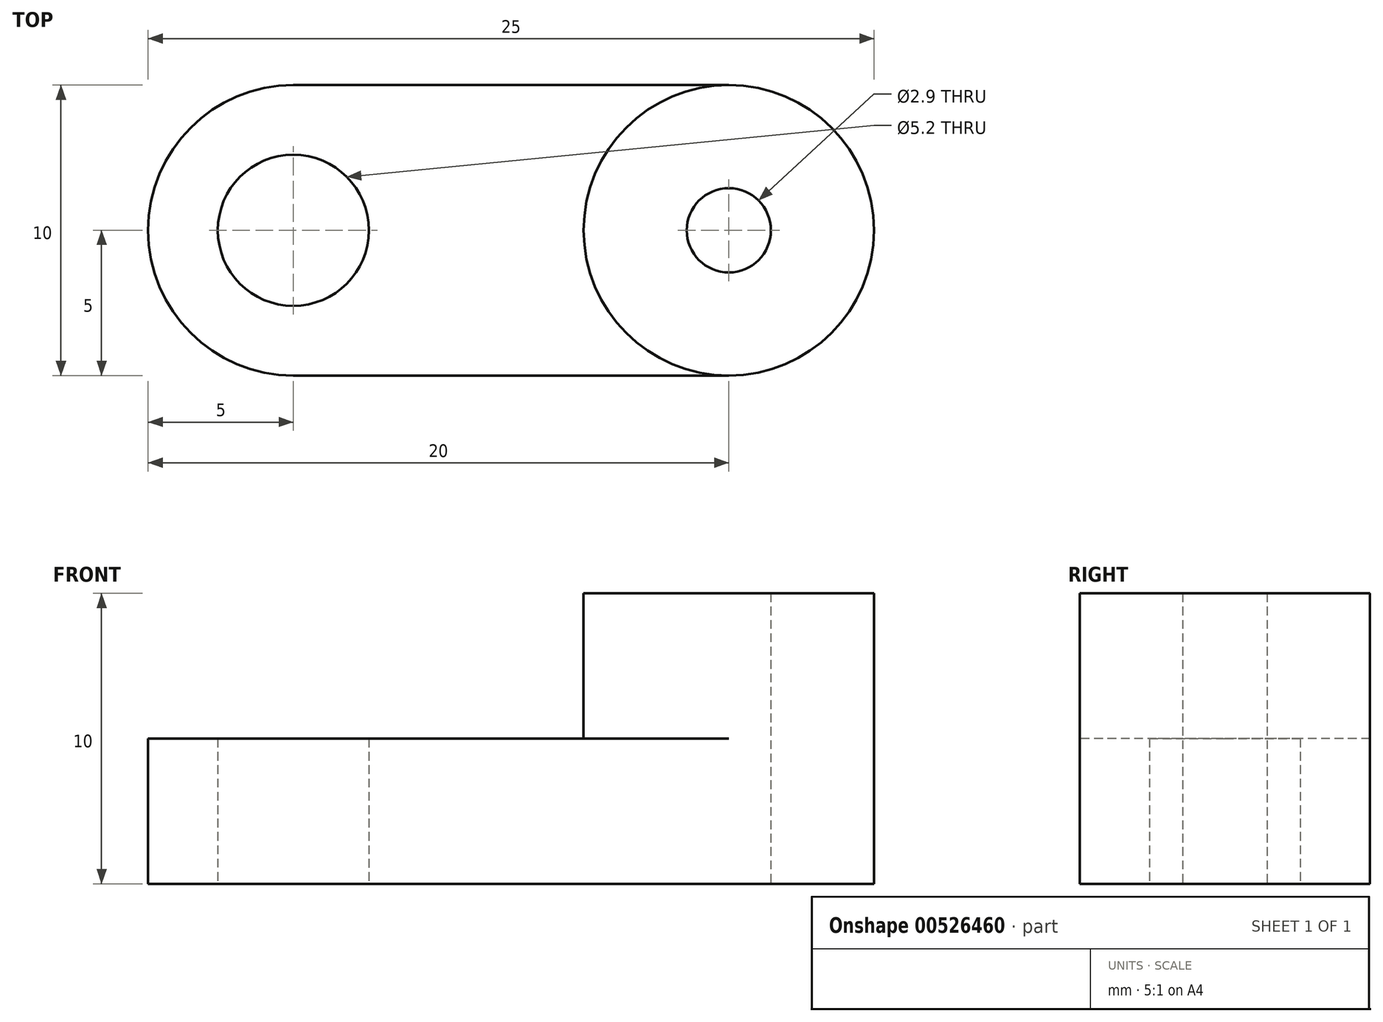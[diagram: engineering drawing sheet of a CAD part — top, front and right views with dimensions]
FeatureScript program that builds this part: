
annotation { "Feature Type Name" : "Feature", "Feature Type Description" : "" }
export const myFeature = defineFeature(function(context is Context, id is Id, definition is map)
    precondition{}
    {
        {
            var Q0;
            Q0=qCreatedBy(makeId("Top.planeOp"),FACE);
            var sketch = newSketch(context, id + "F0", { "sketchPlane" : qUnion([Q0])});
            skLineSegment(sketch, "E0", {"start": v(0, 0) * mm, "end": v(15, 0) * mm});
            skArc(sketch, "E1.0.startCap", {"start": v(0, -5) * mm, "mid": v(-5, 0) * mm, "end": v(0, 5) * mm});
            skArc(sketch, "E1.0.endCap", {"start": v(15, 5) * mm, "mid": v(20, 0) * mm, "end": v(15, -5) * mm});
            skLineSegment(sketch, "E1.0.left", {"start": v(0, 5) * mm, "end": v(15, 5) * mm});
            skLineSegment(sketch, "E1.0.right", {"start": v(0, -5) * mm, "end": v(15, -5) * mm});
            skCircle(sketch, "E2", {"center": v(0, 0) * mm, "radius": 2.6 * mm});
            skCircle(sketch, "E3", {"center": v(15, 0) * mm, "radius": 1.45 * mm});
            skSolve(sketch);
        }
        {
            var Q0;
            Q0 = qSketchRegion(id + "F0", true);
            extrude(context, id + "F1", {"entities" : qUnion([Q0]), "depth" : 5 * mm, "offsetDistance" : 25 * mm});
        }
        {
            var Q0;
            Q0=makeQuery(id+"F1.opExtrude","CAP_FACE",FACE,{"disambiguationData":[OSD([sQuery(id+"F0.wireOp",EDGE,"E1.0.startCap"),sQuery(id+"F0.wireOp",EDGE,"E1.0.endCap"),sQuery(id+"F0.wireOp",EDGE,"E1.0.left"),sQuery(id+"F0.wireOp",EDGE,"E1.0.right"),sQuery(id+"F0.wireOp",EDGE,"E2"),sQuery(id+"F0.wireOp",EDGE,"E3")])],"isStart":false});
            var sketch = newSketch(context, id + "F2", { "sketchPlane" : qUnion([Q0])});
            skCircle(sketch, "E4.0", {"center": v(15, 0) * mm, "radius": 1.45 * mm});
            skCircle(sketch, "E5", {"center": v(15, 0) * mm, "radius": 5 * mm});
            skSolve(sketch);
        }
        {
            var Q0;
            Q0 = qSketchRegion(id + "F2", true);
            extrude(context, id + "F3", {"entities" : qUnion([Q0]), "operationType" : NewBodyOperationType.ADD, "depth" : 5 * mm, "offsetDistance" : 25 * mm});
        }
    });
